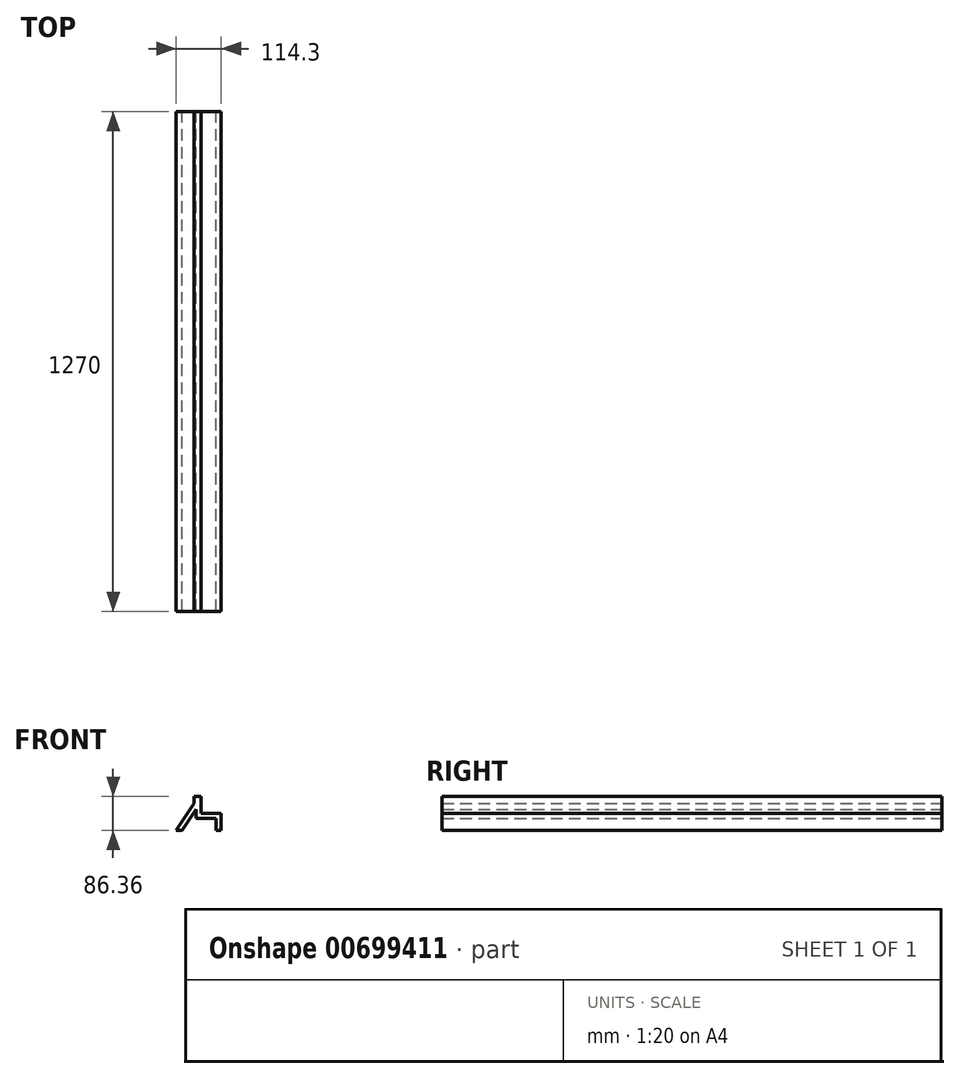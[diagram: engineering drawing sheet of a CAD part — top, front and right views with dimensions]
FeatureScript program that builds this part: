
annotation { "Feature Type Name" : "Feature", "Feature Type Description" : "" }
export const myFeature = defineFeature(function(context is Context, id is Id, definition is map)
    precondition{}
    {
        {
            var Q0;
            Q0=qCreatedBy(makeId("Front.planeOp"),FACE);
            var sketch = newSketch(context, id + "F0", { "sketchPlane" : qUnion([Q0])});
            skLineSegment(sketch, "E0", {"start": v(0, 0) * mm, "end": v(0, 43.18) * mm});
            skLineSegment(sketch, "E1", {"start": v(0, 43.18) * mm, "end": v(-50.8, 43.18) * mm});
            skLineSegment(sketch, "E2", {"start": v(-50.8, 43.18) * mm, "end": v(-50.8, 86.36) * mm});
            skLineSegment(sketch, "E3", {"start": v(-50.8, 86.36) * mm, "end": v(-68.58, 86.36) * mm});
            skLineSegment(sketch, "E4", {"start": v(-68.58, 86.36) * mm, "end": v(-68.58, 68.58) * mm});
            skLineSegment(sketch, "E5", {"start": v(-68.58, 68.58) * mm, "end": v(-114.3, 0) * mm});
            skLineSegment(sketch, "E6", {"start": v(-114.3, 0) * mm, "end": v(-99.04, 0) * mm});
            skLineSegment(sketch, "E7.0", {"start": v(-63.5, 53.3) * mm, "end": v(-99.04, 0) * mm});
            skLineSegment(sketch, "E8.0", {"start": v(-63.5, 30.48) * mm, "end": v(-63.5, 53.3) * mm});
            skLineSegment(sketch, "E9.0", {"start": v(-12.7, 0) * mm, "end": v(-12.7, 30.48) * mm});
            skLineSegment(sketch, "E10.0", {"start": v(-12.7, 30.48) * mm, "end": v(-63.5, 30.48) * mm});
            skLineSegment(sketch, "E11.trimOffspring", {"start": v(-12.7, 0) * mm, "end": v(0, 0) * mm});
            skSolve(sketch);
        }
        {
            var Q0;
            Q0=makeQuery(id+"F0.imprint","IMPRINT",FACE,{"disambiguationData":[TD([[makeQuery(id+"F0.imprint","IMPRINT",EDGE,{"derivedFrom":sQuery(id+"F0.wireOp",EDGE,"E0")}),1.0]])]});
            extrude(context, id + "F1", {"entities" : qUnion([Q0]), "depth" : 1270 * mm, "offsetDistance" : 25.4 * mm});
        }
    });
